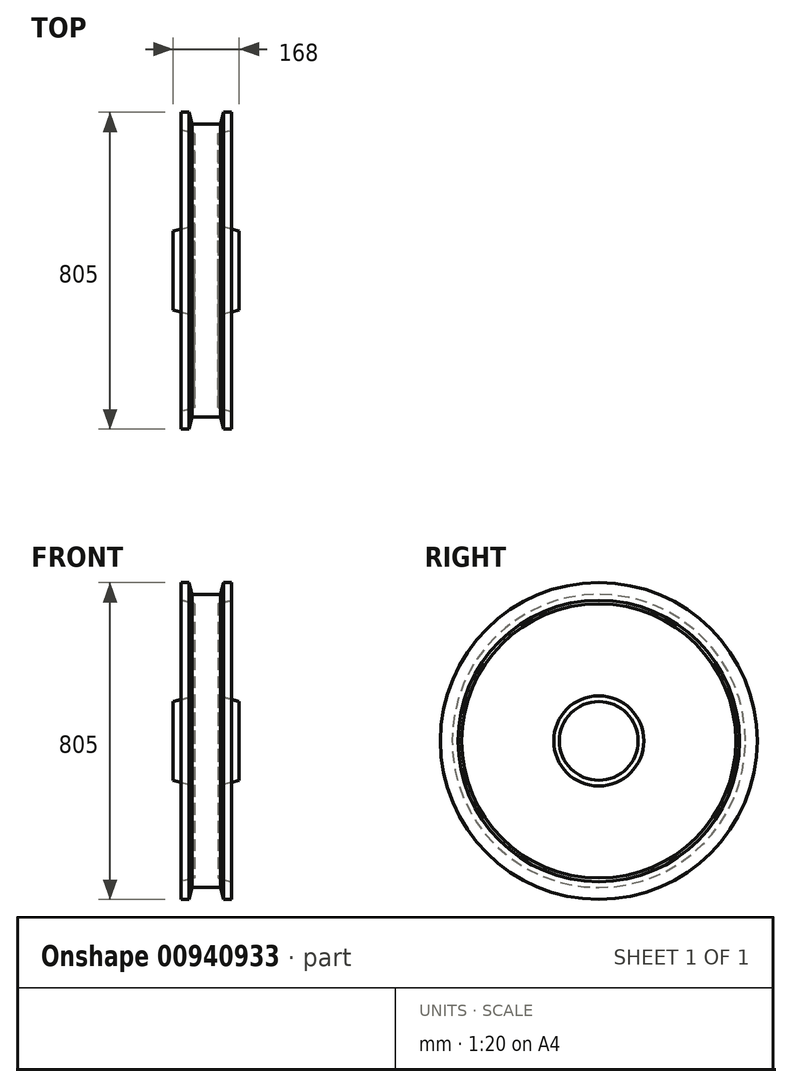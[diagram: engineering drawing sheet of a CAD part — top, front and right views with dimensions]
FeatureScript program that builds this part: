
annotation { "Feature Type Name" : "Feature", "Feature Type Description" : "" }
export const myFeature = defineFeature(function(context is Context, id is Id, definition is map)
    precondition{}
    {
        {
            var Q0;
            Q0=qCreatedBy(makeId("Front.planeOp"),FACE);
            var sketch = newSketch(context, id + "F0", { "sketchPlane" : qUnion([Q0])});
            skLineSegment(sketch, "E0", {"start": v(-84, 0) * mm, "end": v(-84, 100) * mm});
            skLineSegment(sketch, "E1", {"start": v(-84, 100) * mm, "end": v(-30, 114.47) * mm});
            skLineSegment(sketch, "E2", {"start": v(-30, 114.47) * mm, "end": v(-30, 348.39) * mm});
            skLineSegment(sketch, "E3", {"start": v(-30, 348.39) * mm, "end": v(-64, 357.5) * mm});
            skLineSegment(sketch, "E4", {"start": v(-64, 357.5) * mm, "end": v(-64, 402.5) * mm});
            skLineSegment(sketch, "E5", {"start": v(-64, 402.5) * mm, "end": v(-44, 402.5) * mm});
            skLineSegment(sketch, "E6", {"start": v(-44, 402.5) * mm, "end": v(-35.96, 372.5) * mm});
            skLineSegment(sketch, "E7", {"start": v(-35.96, 372.5) * mm, "end": v(0, 372.5) * mm});
            skLineSegment(sketch, "E8", {"start": v(0, 823.4) * mm, "end": v(0, -169.43) * mm, "construction": true});
            skLineSegment(sketch, "E9.MirrorCS", {"start": v(84, 0) * mm, "end": v(84, 100) * mm});
            skLineSegment(sketch, "E10.MirrorCS", {"start": v(84, 100) * mm, "end": v(30, 114.47) * mm});
            skLineSegment(sketch, "E11.MirrorCS", {"start": v(30, 114.47) * mm, "end": v(30, 348.39) * mm});
            skLineSegment(sketch, "E12.MirrorCS", {"start": v(30, 348.39) * mm, "end": v(64, 357.5) * mm});
            skLineSegment(sketch, "E13.MirrorCS", {"start": v(64, 357.5) * mm, "end": v(64, 402.5) * mm});
            skLineSegment(sketch, "E14.MirrorCS", {"start": v(64, 402.5) * mm, "end": v(44, 402.5) * mm});
            skLineSegment(sketch, "E15.MirrorCS", {"start": v(44, 402.5) * mm, "end": v(35.96, 372.5) * mm});
            skLineSegment(sketch, "E16.MirrorCS", {"start": v(35.96, 372.5) * mm, "end": v(0, 372.5) * mm});
            skLineSegment(sketch, "E17", {"start": v(-235.5, 0) * mm, "end": v(280.39, 0) * mm, "construction": true});
            skLineSegment(sketch, "E18", {"start": v(-103.22, 100) * mm, "end": v(119.58, 100) * mm, "construction": true});
            skLineSegment(sketch, "E19", {"start": v(-84, 0) * mm, "end": v(84, 0) * mm});
            skSolve(sketch);
        }
        {
            var Q0;
            Q0=makeQuery(id+"F0.imprint","IMPRINT",FACE,{"disambiguationData":[TD([[makeQuery(id+"F0.imprint","IMPRINT",EDGE,{"derivedFrom":sQuery(id+"F0.wireOp",EDGE,"E0")}),-1.0]])]});
            var Q1;
            Q1=sQuery(id+"F0.wireOp",EDGE,"E17");
            revolve(context, id + "F1", {"surfaceOperationType" : NewSurfaceOperationType.NEW, "entities" : qUnion([Q0]), "axis" : qUnion([Q1]), "revolveType" : RevolveType.FULL});
        }
    });
